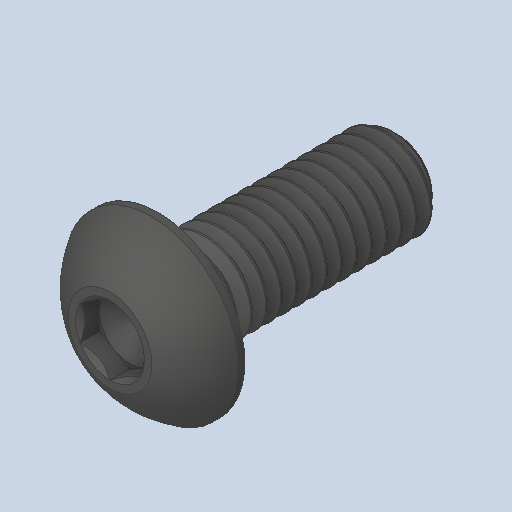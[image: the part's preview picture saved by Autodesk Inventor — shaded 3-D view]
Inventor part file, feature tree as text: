
AUTODESK INVENTOR PART (.ipt)
format: ipt  version: 2023.4 (Build 274418000, 418)  size: 546,304 bytes
history: native  units: in
note: dims shown in document units (in); Inventor stores cm internally (conversion verified against a paired STEP export)
features: revolve x1
ambient origin geometry x8: Origin, YZ Plane, XZ Plane, XY Plane, X Axis, Y Axis, Z Axis, Center Point
bodies: Solid1 (feature_tree)
feature tree (1):
  revolve  "Revolve2"  [1 undecoded]
note: 1 required parameter value undecoded (feature->parameter linkage not recoverable at this tier; creation-order binding heuristic only, values carry confidence <= 0.55)
